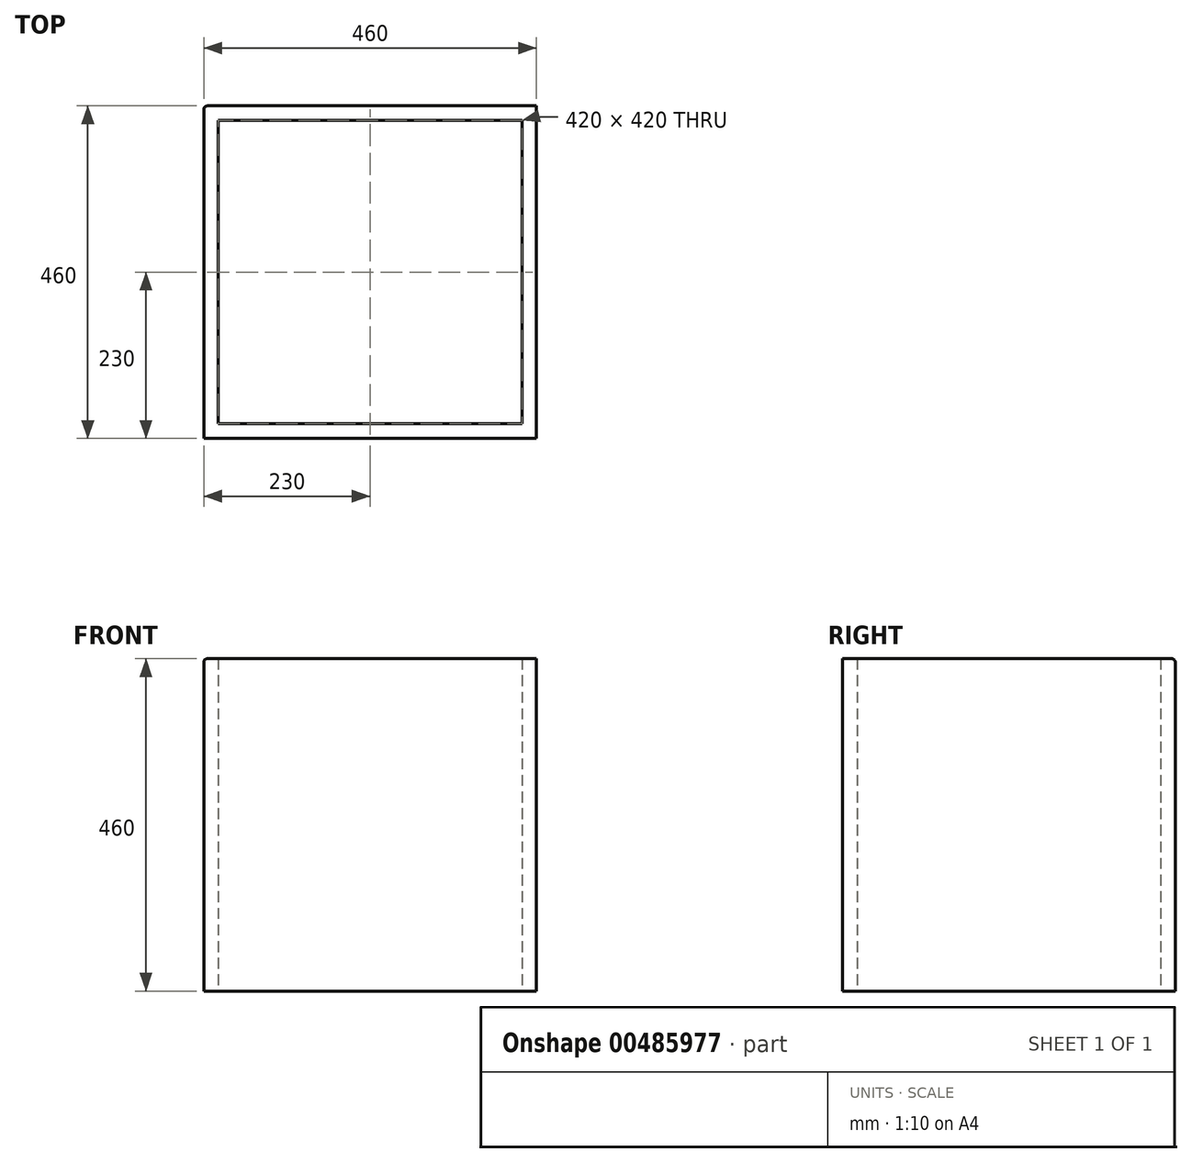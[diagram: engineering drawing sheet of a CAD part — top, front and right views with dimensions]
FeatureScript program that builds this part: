
annotation { "Feature Type Name" : "Feature", "Feature Type Description" : "" }
export const myFeature = defineFeature(function(context is Context, id is Id, definition is map)
    precondition{}
    {
        {
            var Q0;
            Q0=qCreatedBy(makeId("Top.planeOp"),FACE);
            var sketch = newSketch(context, id + "F0", { "sketchPlane" : qUnion([Q0])});
            skCircle(sketch, "E0", {"center": v(0, 0) * mm, "radius": 187 * mm});
            skSolve(sketch);
        }
        {
            var Q0;
            Q0=sQuery(id+"F0.wireOp",EDGE,"E0");
            extrude(context, id + "F1", {"bodyType" : ToolBodyType.SURFACE, "surfaceEntities" : qUnion([Q0]), "depth" : 361 * mm});
        }
        {
            var Q0;
            Q0=qCreatedBy(makeId("Top.planeOp"),FACE);
            var sketch = newSketch(context, id + "F2", { "sketchPlane" : qUnion([Q0])});
            skLineSegment(sketch, "E1.bottom", {"start": v(230, -230) * mm, "end": v(-230, -230) * mm});
            skLineSegment(sketch, "E1.top", {"start": v(230, 230) * mm, "end": v(-230, 230) * mm});
            skLineSegment(sketch, "E1.left", {"start": v(230, -230) * mm, "end": v(230, 230) * mm});
            skLineSegment(sketch, "E1.right", {"start": v(-230, -230) * mm, "end": v(-230, 230) * mm});
            skPoint(sketch, "E1.middle", {"position": v(0, 0) * mm});
            skLineSegment(sketch, "E2.bottom", {"start": v(210, -210) * mm, "end": v(-210, -210) * mm});
            skLineSegment(sketch, "E2.top", {"start": v(210, 210) * mm, "end": v(-210, 210) * mm});
            skLineSegment(sketch, "E2.left", {"start": v(210, -210) * mm, "end": v(210, 210) * mm});
            skLineSegment(sketch, "E2.right", {"start": v(-210, -210) * mm, "end": v(-210, 210) * mm});
            skSolve(sketch);
        }
        {
            var Q0;
            Q0 = qSketchRegion(id + "F2", true);
            extrude(context, id + "F3", {"entities" : qUnion([Q0]), "depth" : 460 * mm});
        }
        {
            var Q0;
            Q0=makeQuery(id+"F3.opExtrude","SWEPT_EDGE",EDGE,{"disambiguationData":[OSD([sQuery(id+"F2.wireOp",EDGE,"E1.top"),sQuery(id+"F2.wireOp",EDGE,"E1.right")])]});
            fillet(context, id + "F4", {"entities" : qUnion([Q0]), "radius" : 5 * mm, "tangentPropagation" : true, "allowEdgeOverflow" : false});
        }
        {
            var Q0;
            Q0=makeQuery(id+"F3.opExtrude","CAP_EDGE",EDGE,{"disambiguationData":[OSD([sQuery(id+"F2.wireOp",EDGE,"E1.right")])],"isStart":false});
            fillet(context, id + "F5", {"entities" : qUnion([Q0]), "radius" : 5 * mm, "tangentPropagation" : true, "allowEdgeOverflow" : false});
        }
    });
